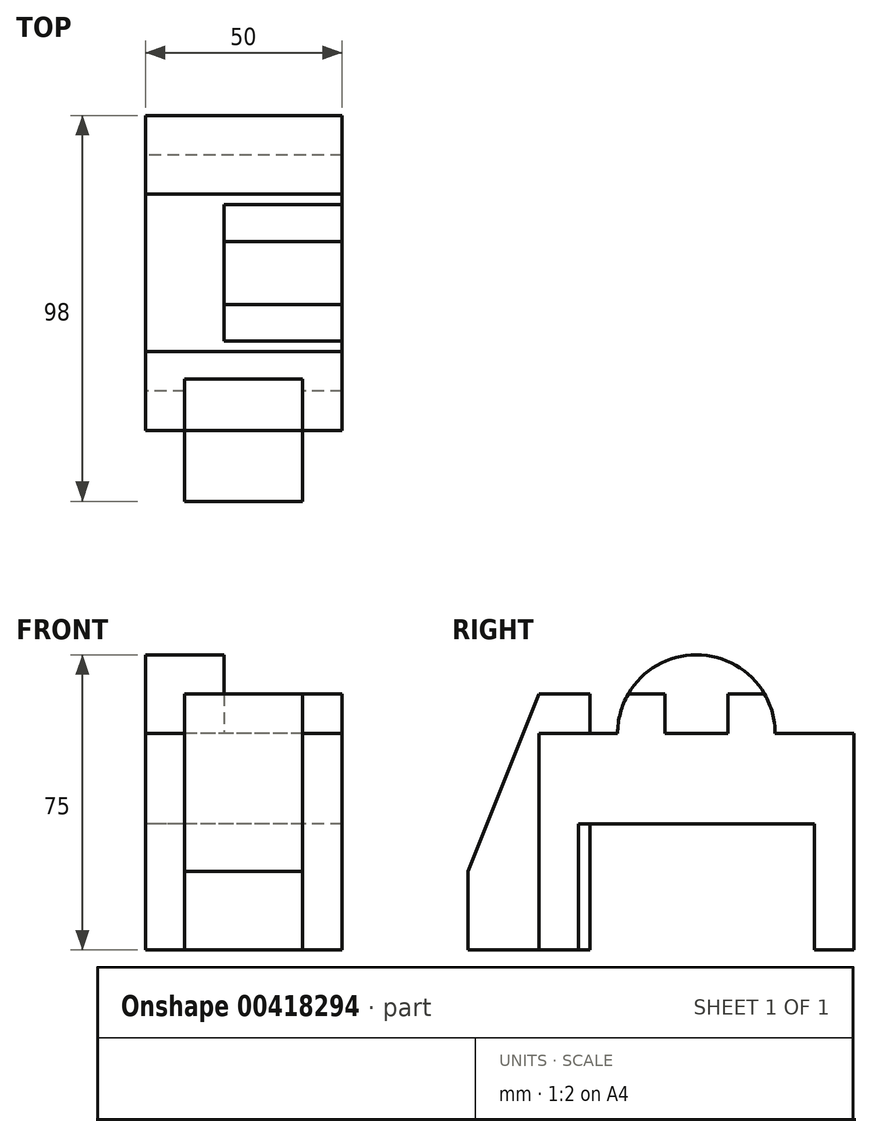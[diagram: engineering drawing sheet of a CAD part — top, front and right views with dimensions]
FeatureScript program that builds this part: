
annotation { "Feature Type Name" : "Feature", "Feature Type Description" : "" }
export const myFeature = defineFeature(function(context is Context, id is Id, definition is map)
    precondition{}
    {
        {
            var Q0;
            Q0=qCreatedBy(makeId("Right.planeOp"),FACE);
            var sketch = newSketch(context, id + "F0", { "sketchPlane" : qUnion([Q0])});
            skLineSegment(sketch, "E0", {"start": v(0, 0) * mm, "end": v(8, 0) * mm});
            skLineSegment(sketch, "E1", {"start": v(8, 0) * mm, "end": v(8, 10) * mm});
            skLineSegment(sketch, "E2", {"start": v(8, 10) * mm, "end": v(17.32, 10) * mm});
            skLineSegment(sketch, "E3", {"start": v(20, 0) * mm, "end": v(40, 0) * mm});
            skLineSegment(sketch, "E4", {"start": v(40, 0) * mm, "end": v(40, -55) * mm});
            skLineSegment(sketch, "E5", {"start": v(40, -55) * mm, "end": v(30, -55) * mm});
            skLineSegment(sketch, "E6", {"start": v(30, -55) * mm, "end": v(30, -23) * mm});
            skLineSegment(sketch, "E7", {"start": v(30, -23) * mm, "end": v(0, -23) * mm});
            skLineSegment(sketch, "E8", {"start": v(0, -23) * mm, "end": v(0, 0) * mm, "construction": true});
            skArc(sketch, "E9", {"start": v(20, 0) * mm, "mid": v(19.32, 5.18) * mm, "end": v(17.32, 10) * mm});
            skLineSegment(sketch, "E10.MirrorCS", {"start": v(-8, 0) * mm, "end": v(-8, 10) * mm});
            skLineSegment(sketch, "E11.MirrorCS", {"start": v(-8, 10) * mm, "end": v(-17.32, 10) * mm});
            skArc(sketch, "E12.MirrorCS", {"start": v(-20, 0) * mm, "mid": v(-19.32, 5.18) * mm, "end": v(-17.32, 10) * mm});
            skLineSegment(sketch, "E13.MirrorCS", {"start": v(-20, 0) * mm, "end": v(-40, 0) * mm});
            skLineSegment(sketch, "E14.MirrorCS", {"start": v(-40, 0) * mm, "end": v(-40, -55) * mm});
            skLineSegment(sketch, "E15.MirrorCS", {"start": v(-40, -55) * mm, "end": v(-30, -55) * mm});
            skLineSegment(sketch, "E16.MirrorCS", {"start": v(-30, -55) * mm, "end": v(-30, -23) * mm});
            skLineSegment(sketch, "E17.MirrorCS", {"start": v(-30, -23) * mm, "end": v(0, -23) * mm});
            skLineSegment(sketch, "E18.MirrorCS", {"start": v(0, 0) * mm, "end": v(-8, 0) * mm});
            skSolve(sketch);
        }
        {
            var Q0;
            Q0 = qSketchRegion(id + "F0", true);
            extrude(context, id + "F1", {"entities" : qUnion([Q0]), "endBound" : BoundingType.SYMMETRIC, "depth" : 50 * mm});
        }
        {
            var Q0;
            Q0=makeQuery(id+"F1.opExtrude","SWEPT_FACE",FACE,{"disambiguationData":[OSD([sQuery(id+"F0.wireOp",EDGE,"E14.MirrorCS")])]});
            var sketch = newSketch(context, id + "F2", { "sketchPlane" : qUnion([Q0])});
            skLineSegment(sketch, "E19.bottom", {"start": v(-15, -55) * mm, "end": v(15, -55) * mm});
            skLineSegment(sketch, "E19.top", {"start": v(-15, 10) * mm, "end": v(15, 10) * mm});
            skLineSegment(sketch, "E19.left", {"start": v(-15, -55) * mm, "end": v(-15, 10) * mm});
            skLineSegment(sketch, "E19.right", {"start": v(15, -55) * mm, "end": v(15, 10) * mm});
            skSolve(sketch);
        }
        {
            var Q0;
            Q0 = qSketchRegion(id + "F2", true);
            extrude(context, id + "F3", {"entities" : qUnion([Q0]), "operationType" : NewBodyOperationType.ADD, "depth" : 18 * mm, "hasSecondDirection" : true, "secondDirectionOppositeDirection" : true, "secondDirectionDepth" : 13 * mm});
        }
        {
            var Q0;
            Q0=makeQuery(id+"F3.opExtrude","CAP_EDGE",EDGE,{"disambiguationData":[OSD([sQuery(id+"F2.wireOp",EDGE,"E19.top")])],"isStart":false});
            chamfer(context, id + "F4", {"entities" : qUnion([Q0]), "chamferType" : ChamferType.TWO_OFFSETS, "width1" : 45 * mm, "oppositeDirection" : true, "width2" : 18 * mm, "tangentPropagation" : true});
        }
        {
            var Q0;
            Q0=makeQuery(id+"F1.opExtrude","CAP_FACE",FACE,{"disambiguationData":[OSD([sQuery(id+"F0.wireOp",EDGE,"E0"),sQuery(id+"F0.wireOp",EDGE,"E1"),sQuery(id+"F0.wireOp",EDGE,"E2"),sQuery(id+"F0.wireOp",EDGE,"E3"),sQuery(id+"F0.wireOp",EDGE,"E4"),sQuery(id+"F0.wireOp",EDGE,"E5"),sQuery(id+"F0.wireOp",EDGE,"E6"),sQuery(id+"F0.wireOp",EDGE,"E7"),sQuery(id+"F0.wireOp",EDGE,"E9"),sQuery(id+"F0.wireOp",EDGE,"E10.MirrorCS"),sQuery(id+"F0.wireOp",EDGE,"E11.MirrorCS"),sQuery(id+"F0.wireOp",EDGE,"E12.MirrorCS"),sQuery(id+"F0.wireOp",EDGE,"E13.MirrorCS"),sQuery(id+"F0.wireOp",EDGE,"E14.MirrorCS"),sQuery(id+"F0.wireOp",EDGE,"E15.MirrorCS"),sQuery(id+"F0.wireOp",EDGE,"E16.MirrorCS"),sQuery(id+"F0.wireOp",EDGE,"E17.MirrorCS"),sQuery(id+"F0.wireOp",EDGE,"E18.MirrorCS")])],"isStart":true});
            var sketch = newSketch(context, id + "F5", { "sketchPlane" : qUnion([Q0])});
            skArc(sketch, "E20", {"start": v(20, 0) * mm, "mid": v(0, 20) * mm, "end": v(-20, 0) * mm});
            skLineSegment(sketch, "E21", {"start": v(-20, 0) * mm, "end": v(20, 0) * mm});
            skSolve(sketch);
        }
        {
            var Q0;
            Q0 = qSketchRegion(id + "F5", true);
            extrude(context, id + "F6", {"entities" : qUnion([Q0]), "operationType" : NewBodyOperationType.ADD, "oppositeDirection" : true, "depth" : 20 * mm});
        }
    });
